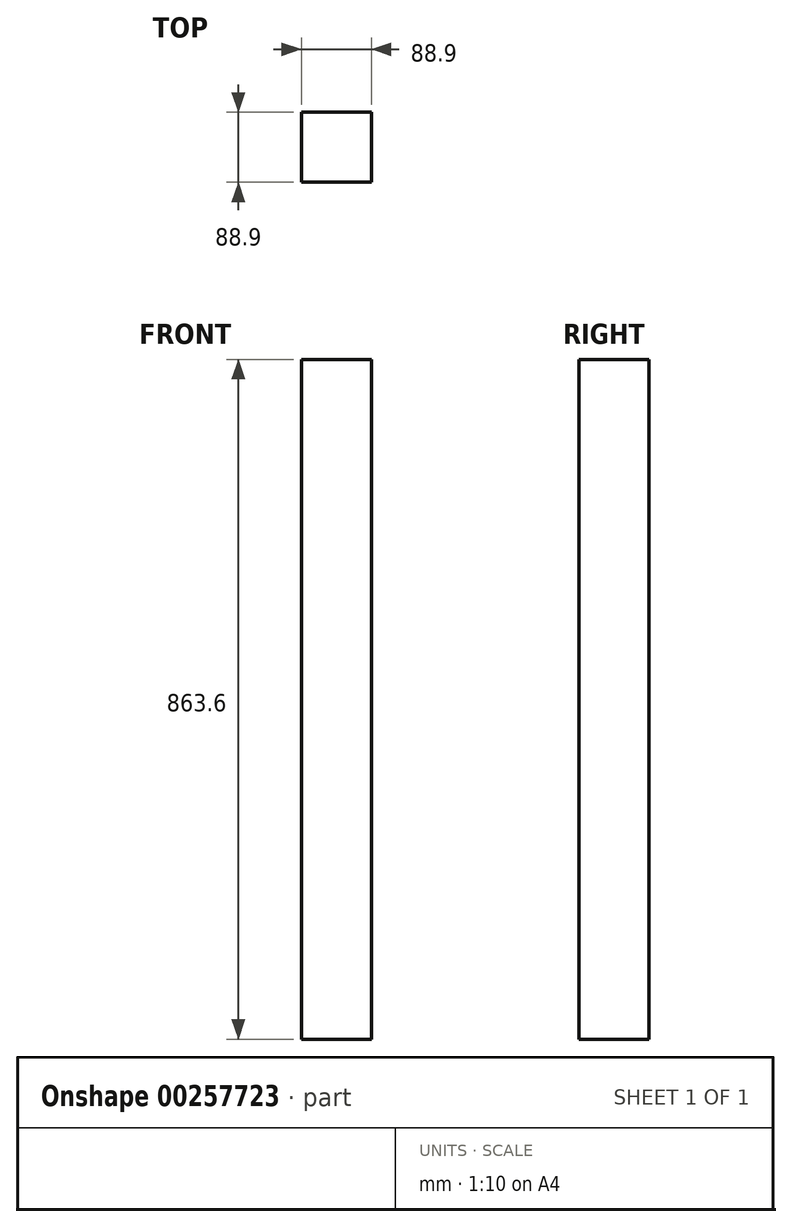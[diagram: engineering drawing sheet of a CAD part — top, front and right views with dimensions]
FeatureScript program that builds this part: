
annotation { "Feature Type Name" : "Feature", "Feature Type Description" : "" }
export const myFeature = defineFeature(function(context is Context, id is Id, definition is map)
    precondition{}
    {
        {
            var Q0;
            Q0=qCreatedBy(makeId("Front.planeOp"),FACE);
            var sketch = newSketch(context, id + "F0", { "sketchPlane" : qUnion([Q0])});
            skLineSegment(sketch, "E0.bottom", {"start": v(-44.45, 431.8) * mm, "end": v(44.45, 431.8) * mm});
            skLineSegment(sketch, "E0.top", {"start": v(-44.45, -431.8) * mm, "end": v(44.45, -431.8) * mm});
            skLineSegment(sketch, "E0.left", {"start": v(-44.45, 431.8) * mm, "end": v(-44.45, -431.8) * mm});
            skLineSegment(sketch, "E0.right", {"start": v(44.45, 431.8) * mm, "end": v(44.45, -431.8) * mm});
            skSolve(sketch);
        }
        {
            var Q0;
            Q0=makeQuery(id+"F0.imprint","IMPRINT",FACE,{"disambiguationData":[TD([[makeQuery(id+"F0.imprint","IMPRINT",EDGE,{"derivedFrom":sQuery(id+"F0.wireOp",EDGE,"E0.bottom")}),-1.0]])]});
            extrude(context, id + "F1", {"entities" : qUnion([Q0]), "endBound" : BoundingType.SYMMETRIC, "depth" : 88.9 * mm});
        }
    });
